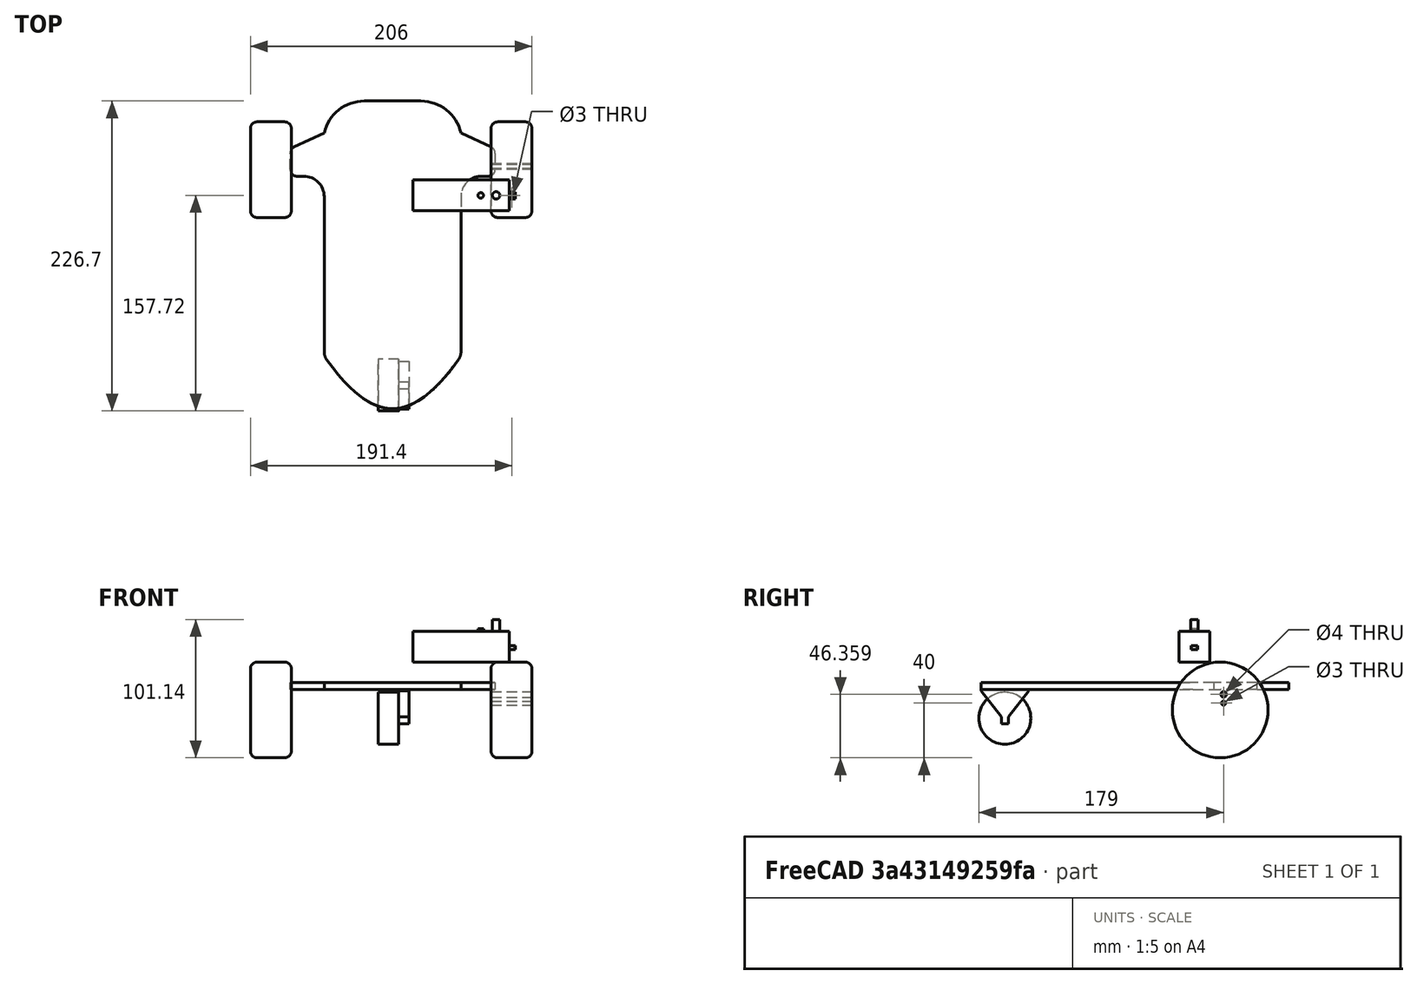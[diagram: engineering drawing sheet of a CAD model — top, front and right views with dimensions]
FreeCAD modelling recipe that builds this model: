
FCSTD DOCUMENT  (FreeCAD 0.19R24291 (Git))
Label: motor
License: All rights reserved
LicenseURL: http://en.wikipedia.org/wiki/All_rights_reserved
objects: Part::Feature×4, Part::Cylinder×3, Part::Box×2, Part::MultiFuse×2, Part::Cut×1, Part::Compound2×1
note: 12 computed .brp shape members not serialized (recipe doc carries the construction recipe); baked Part::Feature solids carry a one-line shape summary decoded from their .brp

FEATURE [Part::Box] Box  label="Base"
  AttacherType = Attacher::AttachEngine3D
  Height = 22.4
  Length = 70.4
  Width = 22.44
FEATURE [Part::Box] Box001  label="Cube001"
  AttacherType = Attacher::AttachEngine3D
  Height = 2.8
  Length = 4.8
  Placement = pos=(70,8.66,9.3) rot=(0,0,1;0rad)
  Width = 5
FEATURE [Part::Cylinder] Cylinder
  Angle = 360
  AttacherType = Attacher::AttachEngine3D
  Height = 10
  Placement = pos=(72.4,11.22,8.3) rot=(0,0,1;0rad)
  Radius = 1.5
FEATURE [Part::Cut] Cut  label="anclaje"
  Base = -> Box001
  Refine = true
  Tool = -> Cylinder
FEATURE [Part::MultiFuse] Fusion
  Refine = true
  Shapes = -> [Cut,Box]
FEATURE [Part::Cylinder] Cylinder001
  Angle = 360
  AttacherType = Attacher::AttachEngine3D
  Height = 8.7
  Placement = pos=(60.75,11.22,22.44) rot=(0,0,1;0rad)
  Radius = 2.7
FEATURE [Part::MultiFuse] Fusion001
  Refine = true
  Shapes = -> [Cylinder001,Fusion]
FEATURE [Part::Cylinder] Cylinder002
  Angle = 360
  AttacherType = Attacher::AttachEngine3D
  Height = 1.92
  Placement = pos=(49.5,11.22,22.44) rot=(0,0,1;0rad)
  Radius = 2
FEATURE [Part::Feature] Solid  label="Rueda Der"
  shape: bbox 30 x 75.77 x 75.77 mm, 7 faces (baked)
FEATURE [Part::Feature] Solid001  label="Rueda loca"
  shape: bbox 22.5 x 38 x 40.07 mm, 13 faces (baked)
FEATURE [Part::Feature] Solid002  label="Rueda Izq"
  shape: bbox 30 x 75.77 x 75.77 mm, 5 faces (baked)
FEATURE [Part::Feature] Solid003  label="Base001"
  shape: bbox 150 x 225.8 x 30 mm, 22 faces (baked)
FEATURE [Part::Compound2] Compound  label="URE->Base v0"
  Links = -> [Solid,Solid001,Solid002,Solid003]
